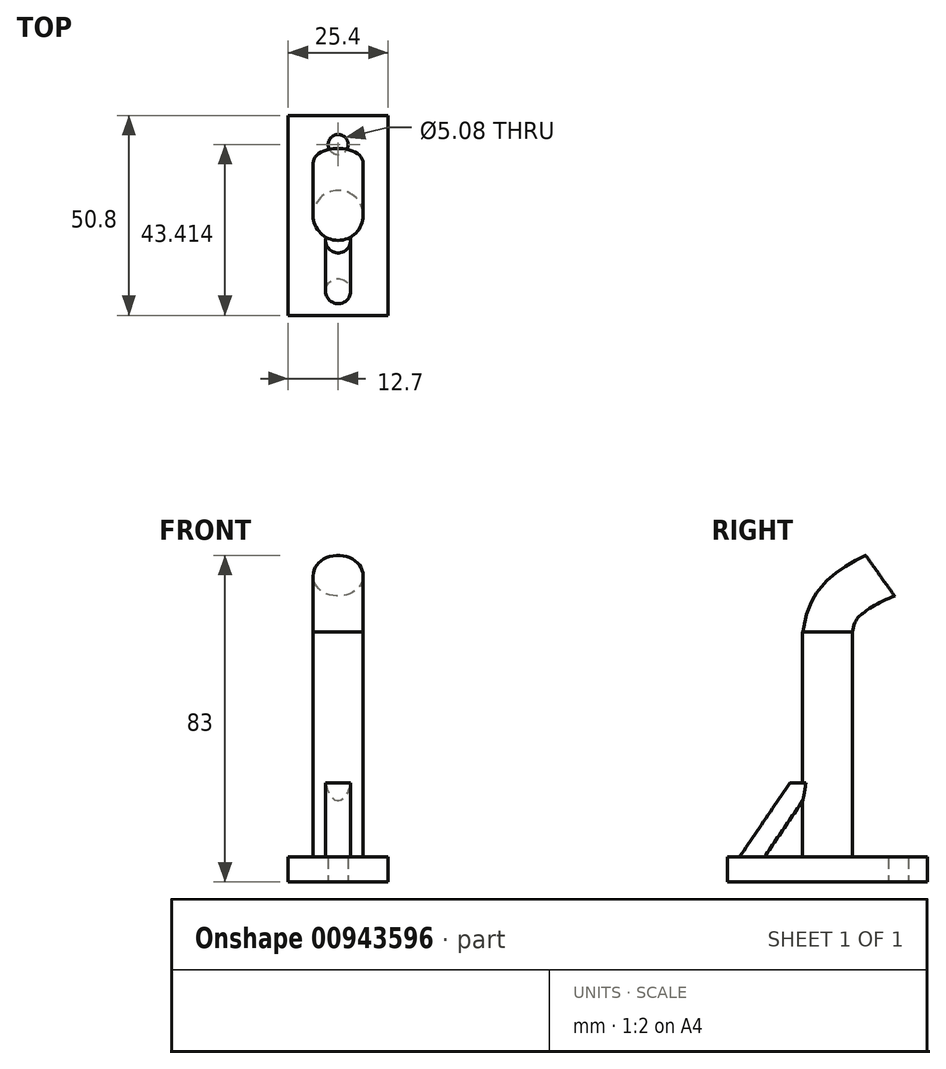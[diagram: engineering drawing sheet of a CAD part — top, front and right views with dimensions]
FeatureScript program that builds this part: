
annotation { "Feature Type Name" : "Feature", "Feature Type Description" : "" }
export const myFeature = defineFeature(function(context is Context, id is Id, definition is map)
    precondition{}
    {
        {
            var Q0;
            Q0=qCreatedBy(makeId("Top.planeOp"),FACE);
            var sketch = newSketch(context, id + "F0", { "sketchPlane" : qUnion([Q0])});
            skLineSegment(sketch, "E0.bottom", {"start": v(-12.7, 25.4) * mm, "end": v(12.7, 25.4) * mm});
            skLineSegment(sketch, "E0.top", {"start": v(-12.7, -25.4) * mm, "end": v(12.7, -25.4) * mm});
            skLineSegment(sketch, "E0.left", {"start": v(-12.7, 25.4) * mm, "end": v(-12.7, -25.4) * mm});
            skLineSegment(sketch, "E0.right", {"start": v(12.7, 25.4) * mm, "end": v(12.7, -25.4) * mm});
            skLineSegment(sketch, "E1", {"start": v(-12.7, 0) * mm, "end": v(12.7, 0) * mm, "construction": true});
            skLineSegment(sketch, "E2", {"start": v(0, 25.4) * mm, "end": v(0, -25.4) * mm, "construction": true});
            skPoint(sketch, "E3", {"position": v(0, 0) * mm});
            skCircle(sketch, "E4", {"center": v(0, 0) * mm, "radius": 6.35 * mm});
            skCircle(sketch, "E5", {"center": v(0, 18.01) * mm, "radius": 2.54 * mm});
            skCircle(sketch, "E6", {"center": v(0, -19.26) * mm, "radius": 3.18 * mm});
            skSolve(sketch);
        }
        {
            var Q0;
            Q0=makeQuery(id+"F0.imprint","IMPRINT",FACE,{"disambiguationData":[TD([[makeQuery(id+"F0.imprint","IMPRINT",EDGE,{"derivedFrom":sQuery(id+"F0.wireOp",EDGE,"E0.bottom")}),-1.0]])]});
            extrude(context, id + "F1", {"entities" : qUnion([Q0]), "depth" : 6.35 * mm, "offsetDistance" : 25.4 * mm});
        }
        {
            var Q0;
            Q0=makeQuery(id+"F0.imprint","IMPRINT",FACE,{"disambiguationData":[TD([[makeQuery(id+"F0.imprint","IMPRINT",EDGE,{"derivedFrom":sQuery(id+"F0.wireOp",EDGE,"E4")}),1.0]])]});
            extrude(context, id + "F2", {"entities" : qUnion([Q0]), "operationType" : NewBodyOperationType.ADD, "depth" : 63.5 * mm, "offsetDistance" : 25.4 * mm});
        }
        {
            var Q0;
            Q0=qCreatedBy(makeId("Right.planeOp"),FACE);
            var sketch = newSketch(context, id + "F3", { "sketchPlane" : qUnion([Q0])});
            skLineSegment(sketch, "E7.0", {"start": v(25.4, 0) * mm, "end": v(-25.4, 0) * mm, "construction": true});
            skLineSegment(sketch, "E8", {"start": v(-22.43, 0) * mm, "end": v(-22.43, 6.35) * mm, "construction": true});
            skLineSegment(sketch, "E9", {"start": v(-16.08, 6.35) * mm, "end": v(-16.08, 0) * mm, "construction": true});
            skLineSegment(sketch, "E10.0", {"start": v(-22.43, 6.35) * mm, "end": v(-16.08, 6.35) * mm, "construction": true});
            skLineSegment(sketch, "E11", {"start": v(-6.35, 6.35) * mm, "end": v(-6.35, 63.5) * mm, "construction": true});
            skLineSegment(sketch, "E12", {"start": v(6.35, 63.5) * mm, "end": v(6.35, 6.35) * mm, "construction": true});
            skLineSegment(sketch, "E13", {"start": v(-19.26, 6.35) * mm, "end": v(-19.26, 25.27) * mm, "construction": true});
            skLineSegment(sketch, "E14", {"start": v(-19.26, 25.27) * mm, "end": v(-6.35, 25.27) * mm, "construction": true});
            skLineSegment(sketch, "E15", {"start": v(-19.26, 6.35) * mm, "end": v(-6.35, 25.27) * mm});
            skLineSegment(sketch, "E16.0", {"start": v(-22.43, 6.35) * mm, "end": v(-16.08, 6.35) * mm});
            skLineSegment(sketch, "E17.0", {"start": v(-6.35, 63.5) * mm, "end": v(6.35, 63.5) * mm});
            skFitSpline(sketch, "E18", {"points": [v(0, 63.5) * mm, v(2, 69.48) * mm, v(13.34, 77.83) * mm], "startDerivative": vector(2.62, 10.72) * mm, "endDerivative": vector(23.81, 9.52) * mm});
            skSolve(sketch);
        }
        {
            var Q0;
            Q0=makeQuery(id+"F0.imprint","IMPRINT",FACE,{"disambiguationData":[TD([[makeQuery(id+"F0.imprint","IMPRINT",EDGE,{"derivedFrom":sQuery(id+"F0.wireOp",EDGE,"E6")}),1.0]])]});
            var Q1;
            Q1=makeQuery(id+"F1.opExtrude","CAP_FACE",FACE,{"disambiguationData":[OSD([sQuery(id+"F0.wireOp",EDGE,"E0.bottom"),sQuery(id+"F0.wireOp",EDGE,"E0.top"),sQuery(id+"F0.wireOp",EDGE,"E0.left"),sQuery(id+"F0.wireOp",EDGE,"E0.right"),sQuery(id+"F0.wireOp",EDGE,"E4"),sQuery(id+"F0.wireOp",EDGE,"E5"),sQuery(id+"F0.wireOp",EDGE,"E6")])],"isStart":false});
            extrude(context, id + "F4", {"entities" : qUnion([Q0]), "operationType" : NewBodyOperationType.ADD, "endBound" : BoundingType.UP_TO_SURFACE, "depth" : 25.4 * mm, "endBoundEntityFace" : qUnion([Q1]), "offsetDistance" : 25.4 * mm});
        }
        {
            var Q0;
            Q0=makeQuery(id+"F2.opExtrude","CAP_FACE",FACE,{"disambiguationData":[OSD([sQuery(id+"F0.wireOp",EDGE,"E4")])],"isStart":false});
            var Q1;
            Q1=sQuery(id+"F3.wireOp",EDGE,"E18");
            sweep(context, id + "F5", {"operationType" : NewBodyOperationType.ADD, "profiles" : qUnion([Q0]), "path" : qUnion([Q1])});
        }
        {
            var Q0;
            {var subQ0=sQuery(id+"F0.wireOp",EDGE,"E6");Q0=makeQuery(id+"F4.boolean.opBoolean","MERGE",FACE,{"derivedFrom":[makeQuery(id+"F1.opExtrude","CAP_FACE",FACE,{"disambiguationData":[OSD([sQuery(id+"F0.wireOp",EDGE,"E0.bottom"),sQuery(id+"F0.wireOp",EDGE,"E0.top"),sQuery(id+"F0.wireOp",EDGE,"E0.left"),sQuery(id+"F0.wireOp",EDGE,"E0.right"),sQuery(id+"F0.wireOp",EDGE,"E4"),sQuery(id+"F0.wireOp",EDGE,"E5"),subQ0])],"isStart":false}),makeQuery(id+"F4.opExtrude","CAP_FACE",FACE,{"disambiguationData":[OSD([subQ0])],"isStart":false})]});}
            var sketch = newSketch(context, id + "F6", { "sketchPlane" : qUnion([Q0])});
            skCircle(sketch, "E19.0", {"center": v(0, -19.26) * mm, "radius": 3.18 * mm});
            skSolve(sketch);
        }
        {
            var Q0;
            Q0=makeQuery(id+"F6.imprint","IMPRINT",FACE,{"disambiguationData":[TD([[makeQuery(id+"F6.imprint","IMPRINT",EDGE,{"derivedFrom":sQuery(id+"F6.wireOp",EDGE,"E19.0")}),1.0]])]});
            var Q1;
            Q1=sQuery(id+"F3.wireOp",EDGE,"E15");
            sweep(context, id + "F7", {"operationType" : NewBodyOperationType.ADD, "profiles" : qUnion([Q0]), "path" : qUnion([Q1])});
        }
    });
